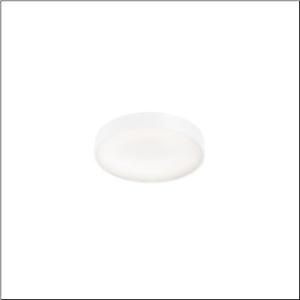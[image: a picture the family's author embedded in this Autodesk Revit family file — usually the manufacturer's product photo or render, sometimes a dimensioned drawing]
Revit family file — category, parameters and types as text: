
# Revit family: round_21_s_51mr34nd0321w
name_source: partatom
category: Lighting Fixtures
units: mm (PartAtom-declared; Revit-internal decimal feet)

## family parameters
Cut with Voids When Loaded = No
Host = Face
Light Source = No
Part Type = Normal
Room Calculation Point = No
Round Connector Dimension = Use Diameter
Shared = No

## types (1)
- Round 21 S (1 x LED, 3660 lm, 28.3 W, 3000K)
    Apparent Load = 28 VA
    CIE Flux Codes = 66 90 98 71 100
    Color Rendering = 80
    Color Temperature = 3000K
    Default Elevation = 1800 mm
    Description = Round 21 S, wall and ceiling luminaire, primary optical cover: micro prismatic cover, of PMMA, transparent, CAT 2 (L<= 3000cd/m²), light emission: direct/indirect distribution, primary light characteristic: symmetric, installation type: suspended mounting, surface-mounted, LED, rated luminous flux: 3.660lm, luminous efficacy: 129lm/W, light colour: 830, colour temperature: 3000K, control gear: DALI 2, with terminal, 5-pole, mains connection: 230V, AC, 50/60Hz, rated input power: 28.3W, housing, of aluminium, coated, white, diameter: 400mm, height: 62mm, protection rating (complete): IP40, insulation class (complete): insulation class I (protective earthing), certification: CE, impact resistance: IK04, permissible operating ambient temperature: -10..+35°C, packaging unit: 1 piece
    Height = 87 mm
    Lamp = 1 x LED
    Lamp Light Flux = 3660 lm
    Lamp Power = 28.3 W
    Lamp count = 1
    Length = 400 mm
    Luminous efficacy = 129 lm/W
    Manufacturer = Siteco
    ModVariant = No
    Model = 51MR34ND0321W
    Mounting Place = Ceiling
    Mounting Type = Surface mounted
    Number of Poles = 1
    OnlyDefault = Yes
    Power Factor = 1
    Product Name = Round 21 S
    Product group = wall and ceiling luminaire | ceiling mounted
    ProductGroupID = 304
    Protection Class = Protection class I
    Protection Degree = IP 40
    RLX_Detail_Level = 1
    RLX_Emergency_Light_Flux = 0 lm
    RLX_Emergency_Type = 0
    RLX_Emergency_Type_DB = No
    RlxData = <blob elided: 12841 chars, md5=bb697be6>
    Socket = socket
    Standby Power = 0 W
    System Light Flux = 3660 lm
    System Power = 28 W
    Type Comments = Product without accessories
    Type Image = l_1258334.jpg
    URL = http://relux.com
    VarID = ---
    Voltage = 0 V
    Weight = 0.00 kg
    Width = 0 mm  [stored 0 ft]

note: [stored X ft] marks values corroborated as IEEE doubles in the binary element streams (Revit-internal decimal feet)

## geometry (parser evidence)
native form markers: Sweep x10
no freeform markers — native parametric forms only
